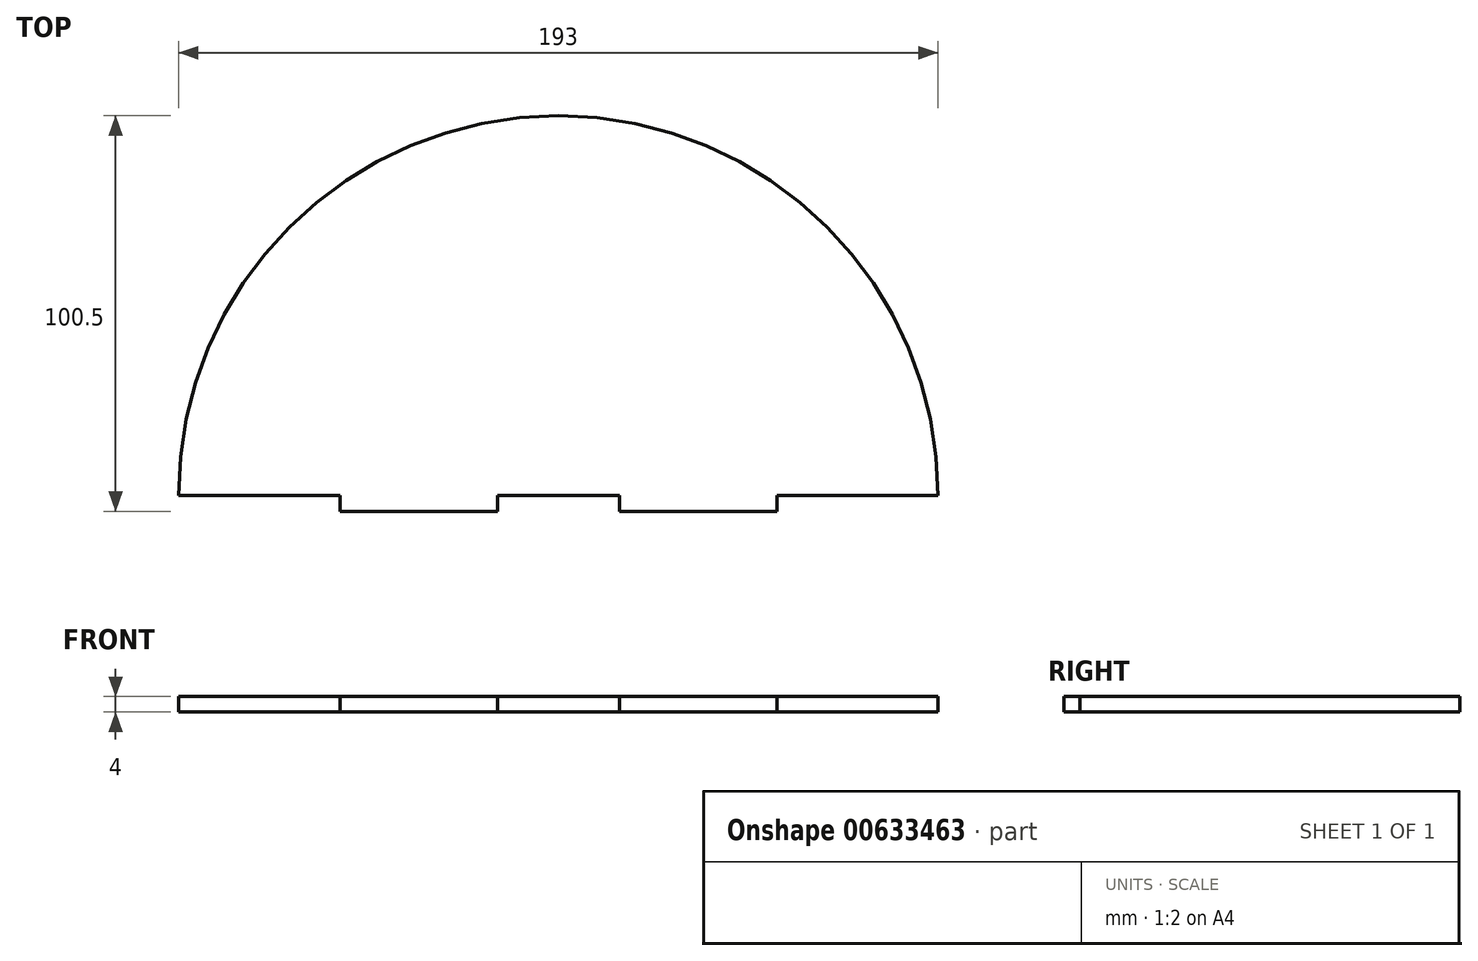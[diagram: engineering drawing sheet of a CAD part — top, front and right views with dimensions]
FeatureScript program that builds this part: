
annotation { "Feature Type Name" : "Feature", "Feature Type Description" : "" }
export const myFeature = defineFeature(function(context is Context, id is Id, definition is map)
    precondition{}
    {
        {
            var Q0;
            Q0=qCreatedBy(makeId("Top.planeOp"),FACE);
            var sketch = newSketch(context, id + "F0", { "sketchPlane" : qUnion([Q0])});
            skArc(sketch, "E0", {"start": v(96.5, 0) * mm, "mid": v(0, 96.5) * mm, "end": v(-96.5, 0) * mm});
            skLineSegment(sketch, "E1.bottom", {"start": v(-96.5, 0) * mm, "end": v(96.5, 0) * mm});
            skPoint(sketch, "E1.left.start.orphan", {"position": v(-111.67, 0) * mm});
            skSolve(sketch);
        }
        {
            var Q0;
            Q0 = qSketchRegion(id + "F0", true);
            extrude(context, id + "F1", {"entities" : qUnion([Q0]), "depth" : 4 * mm, "offsetDistance" : 25 * mm});
        }
        {
            var Q0;
            Q0=qCreatedBy(makeId("Top.planeOp"),FACE);
            var sketch = newSketch(context, id + "F2", { "sketchPlane" : qUnion([Q0])});
            skLineSegment(sketch, "E2.bottom", {"start": v(-55.5, 0) * mm, "end": v(-15.5, 0) * mm});
            skLineSegment(sketch, "E2.top", {"start": v(-55.5, -4) * mm, "end": v(-15.5, -4) * mm});
            skLineSegment(sketch, "E2.left", {"start": v(-55.5, 0) * mm, "end": v(-55.5, -4) * mm});
            skLineSegment(sketch, "E2.right", {"start": v(-15.5, 0) * mm, "end": v(-15.5, -4) * mm});
            skLineSegment(sketch, "E3.bottom", {"start": v(15.5, 0) * mm, "end": v(55.5, 0) * mm});
            skLineSegment(sketch, "E3.top", {"start": v(15.5, -4) * mm, "end": v(55.5, -4) * mm});
            skLineSegment(sketch, "E3.left", {"start": v(15.5, 0) * mm, "end": v(15.5, -4) * mm});
            skLineSegment(sketch, "E3.right", {"start": v(55.5, 0) * mm, "end": v(55.5, -4) * mm});
            skSolve(sketch);
        }
        {
            var Q0;
            Q0 = qSketchRegion(id + "F2", true);
            extrude(context, id + "F3", {"entities" : qUnion([Q0]), "operationType" : NewBodyOperationType.ADD, "depth" : 4 * mm, "offsetDistance" : 25 * mm});
        }
    });
